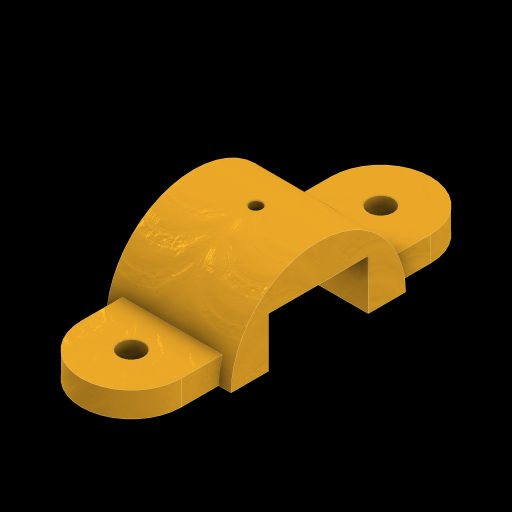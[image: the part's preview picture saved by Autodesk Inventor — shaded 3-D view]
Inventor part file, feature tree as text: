
AUTODESK INVENTOR PART (.ipt)
format: ipt  version: 2024 (Build 280153000, 153)  size: 215,552 bytes
history: native  units: in
note: dims shown in document units (in); Inventor stores cm internally (conversion verified against a paired STEP export)
features: extrude x6, sketch x5
ambient origin geometry x8: Origin, YZ Plane, XZ Plane, XY Plane, X Axis, Y Axis, Z Axis, Center Point
bodies: Solid1 (feature_tree)
feature tree (11):
  extrude  "BASE"  Depth=0.5in
  sketch  "Sketch2"  dims[d2=0.5in d3=1.0in]
  extrude  "REMOVED CENTER OF BASE"  Depth=1.0in
  extrude  "ARCH"  Depth=1.75in
  extrude  "TOPHOLE"  TaperAngle=0.0deg  [1 undecoded]
  extrude  "CIRCULAR"  Depth=0.25in
  extrude  "SQUARE"  TaperAngle=0.0deg  [1 undecoded]
  sketch  "Sketch1"  dims[d0=5.0in d1=0.5in]
  sketch  "Sketch3"  dims[d5=0.5in d6=0.0in d7=1.75in]
  sketch  "Sketch5"  dims[d8=1.25in d9=0.0in d10=0.0in]
  sketch  "Sketch6"  dims[d11=2.5in d12=0.0in d13=0.25in d14=0.0in d15=0.0in d16=2.5in d17=1.25in d18=0.625in d19=0.0in d20=0.0in d21=2.5in d22=0.0in d23=2.0in d24=1.0in d25=1.0in d26=1.25in]
note: 2 required parameter values undecoded (feature->parameter linkage not recoverable at this tier; creation-order binding heuristic only, values carry confidence <= 0.55)
